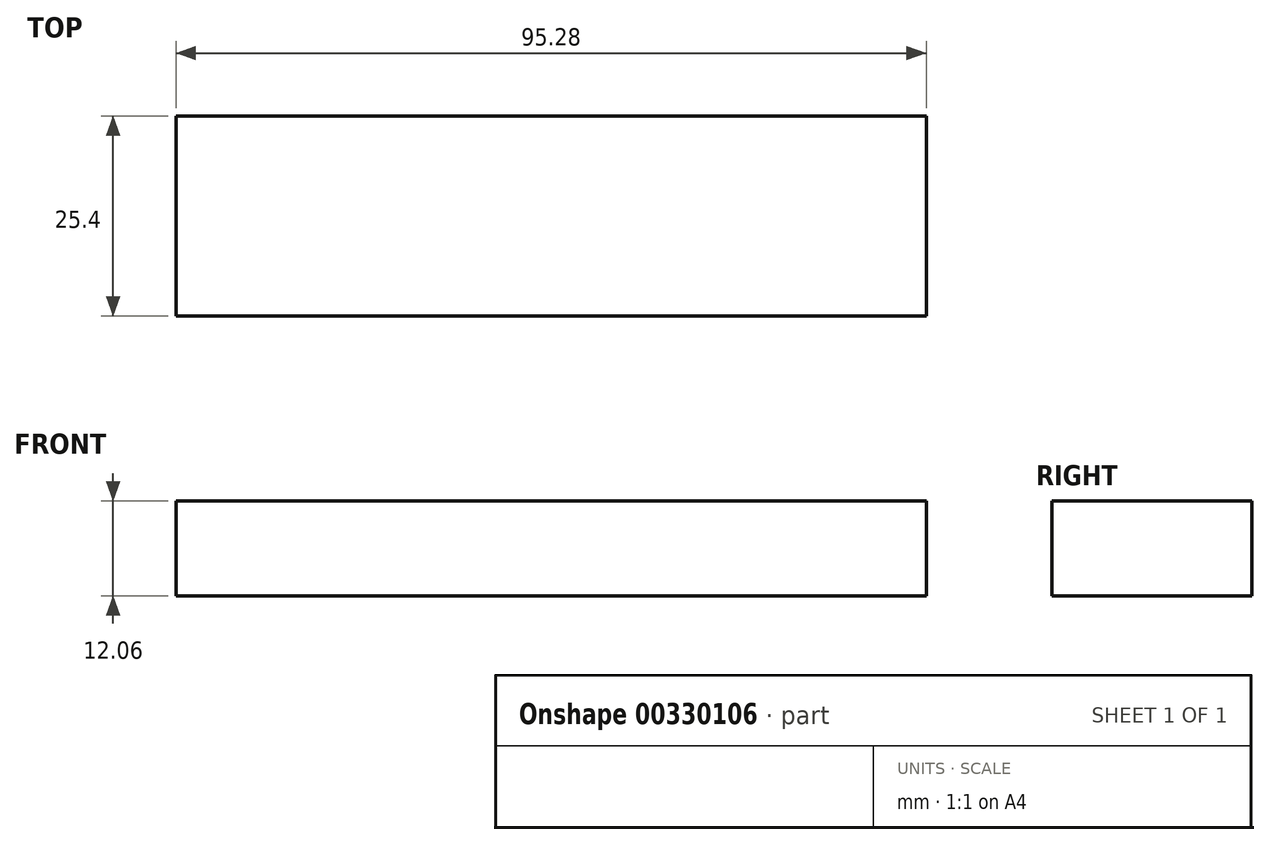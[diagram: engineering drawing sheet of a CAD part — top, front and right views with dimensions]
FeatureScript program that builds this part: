
annotation { "Feature Type Name" : "Feature", "Feature Type Description" : "" }
export const myFeature = defineFeature(function(context is Context, id is Id, definition is map)
    precondition{}
    {
        {
            var Q0;
            Q0=qCreatedBy(makeId("Front.planeOp"),FACE);
            var sketch = newSketch(context, id + "F0", { "sketchPlane" : qUnion([Q0])});
            skLineSegment(sketch, "E0.left", {"start": v(0, 0) * mm, "end": v(0, -3.68) * mm});
            skLineSegment(sketch, "E0.right", {"start": v(19.96, 0) * mm, "end": v(19.96, -3.68) * mm});
            skLineSegment(sketch, "E1.bottom", {"start": v(47.64, 6.03) * mm, "end": v(-47.64, 6.03) * mm});
            skLineSegment(sketch, "E1.top", {"start": v(47.64, -6.03) * mm, "end": v(-47.64, -6.03) * mm});
            skLineSegment(sketch, "E1.left", {"start": v(47.64, 6.03) * mm, "end": v(47.64, -6.03) * mm});
            skLineSegment(sketch, "E1.right", {"start": v(-47.64, 6.03) * mm, "end": v(-47.64, -6.03) * mm});
            skPoint(sketch, "E1.middle", {"position": v(0, 0) * mm});
            skSolve(sketch);
        }
        {
            var Q0;
            Q0=makeQuery(id+"F0.imprint","IMPRINT",FACE,{"disambiguationData":[TD([[makeQuery(id+"F0.imprint","IMPRINT",EDGE,{"derivedFrom":sQuery(id+"F0.wireOp",EDGE,"E1.bottom")}),1.0]])]});
            extrude(context, id + "F1", {"entities" : qUnion([Q0]), "depth" : 25.4 * mm});
        }
    });
